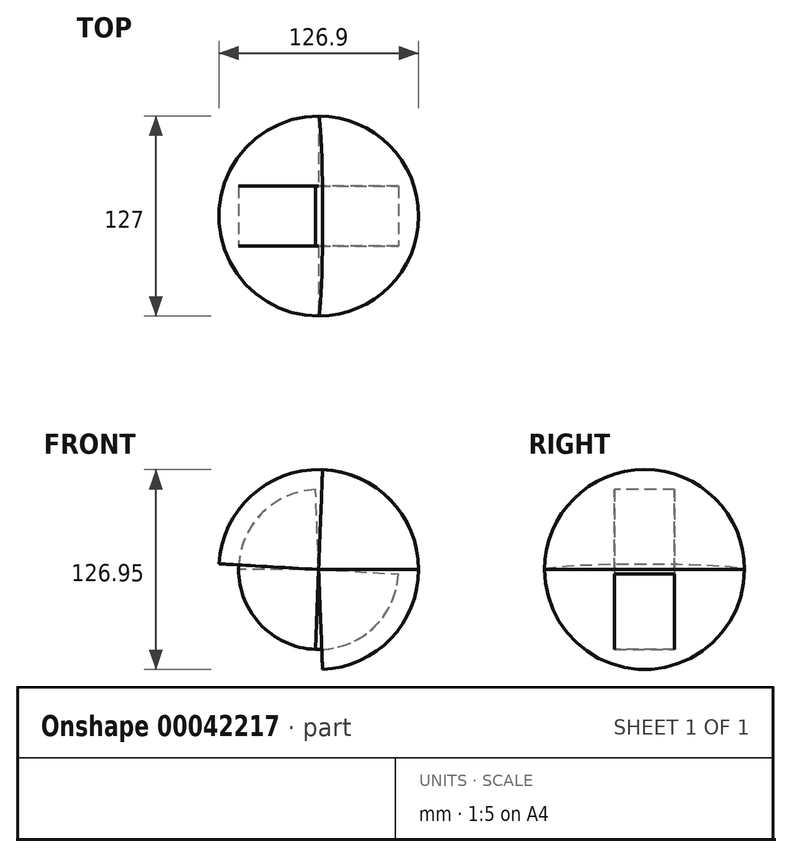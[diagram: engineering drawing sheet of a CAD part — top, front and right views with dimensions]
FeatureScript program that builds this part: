
annotation { "Feature Type Name" : "Feature", "Feature Type Description" : "" }
export const myFeature = defineFeature(function(context is Context, id is Id, definition is map)
    precondition{}
    {
        {
            var Q0;
            Q0=qCreatedBy(makeId("Top.planeOp"),FACE);
            var sketch = newSketch(context, id + "F0", { "sketchPlane" : qUnion([Q0])});
            skArc(sketch, "E0", {"start": v(0, -63.5) * mm, "mid": v(63.5, 0) * mm, "end": v(0, 63.5) * mm});
            skLineSegment(sketch, "E1", {"start": v(0, 63.5) * mm, "end": v(0, 19.05) * mm});
            skLineSegment(sketch, "E2", {"start": v(0, 19.05) * mm, "end": v(-50.8, 19.05) * mm});
            skLineSegment(sketch, "E3", {"start": v(0, -19.05) * mm, "end": v(-50.8, -19.05) * mm});
            skLineSegment(sketch, "E4", {"start": v(-50.8, 19.05) * mm, "end": v(-50.8, -19.05) * mm});
            skLineSegment(sketch, "E5.trimOffspring", {"start": v(0, -19.05) * mm, "end": v(0, -63.5) * mm});
            skSolve(sketch);
        }
        {
            var Q0;
            Q0=qCreatedBy(makeId("Right.planeOp"),FACE);
            var sketch = newSketch(context, id + "F1", { "sketchPlane" : qUnion([Q0])});
            skLineSegment(sketch, "E6", {"start": v(75.84, 0) * mm, "end": v(-76.73, 0) * mm});
            skSolve(sketch);
        }
        {
            var Q0;
            Q0=makeQuery(id+"F0.imprint","IMPRINT",FACE,{"disambiguationData":[TD([[makeQuery(id+"F0.imprint","IMPRINT",EDGE,{"derivedFrom":sQuery(id+"F0.wireOp",EDGE,"E0")}),1.0]])]});
            var Q1;
            Q1=sQuery(id+"F1.wireOp",EDGE,"E6");
            revolve(context, id + "F2", {"entities" : qUnion([Q0]), "axis" : qUnion([Q1]), "revolveType" : RevolveType.ONE_DIRECTION, "angle" : 176.75 * degree});
        }
        {
            var Q0;
            Q0 = qSketchRegion(id + "F0", true);
            var Q1;
            Q1=sQuery(id+"F1.wireOp",EDGE,"E6");
            revolve(context, id + "F3", {"entities" : qUnion([Q0]), "axis" : qUnion([Q1]), "revolveType" : RevolveType.SYMMETRIC, "oppositeDirection" : true, "angle" : 175.53 * degree});
        }
    });
